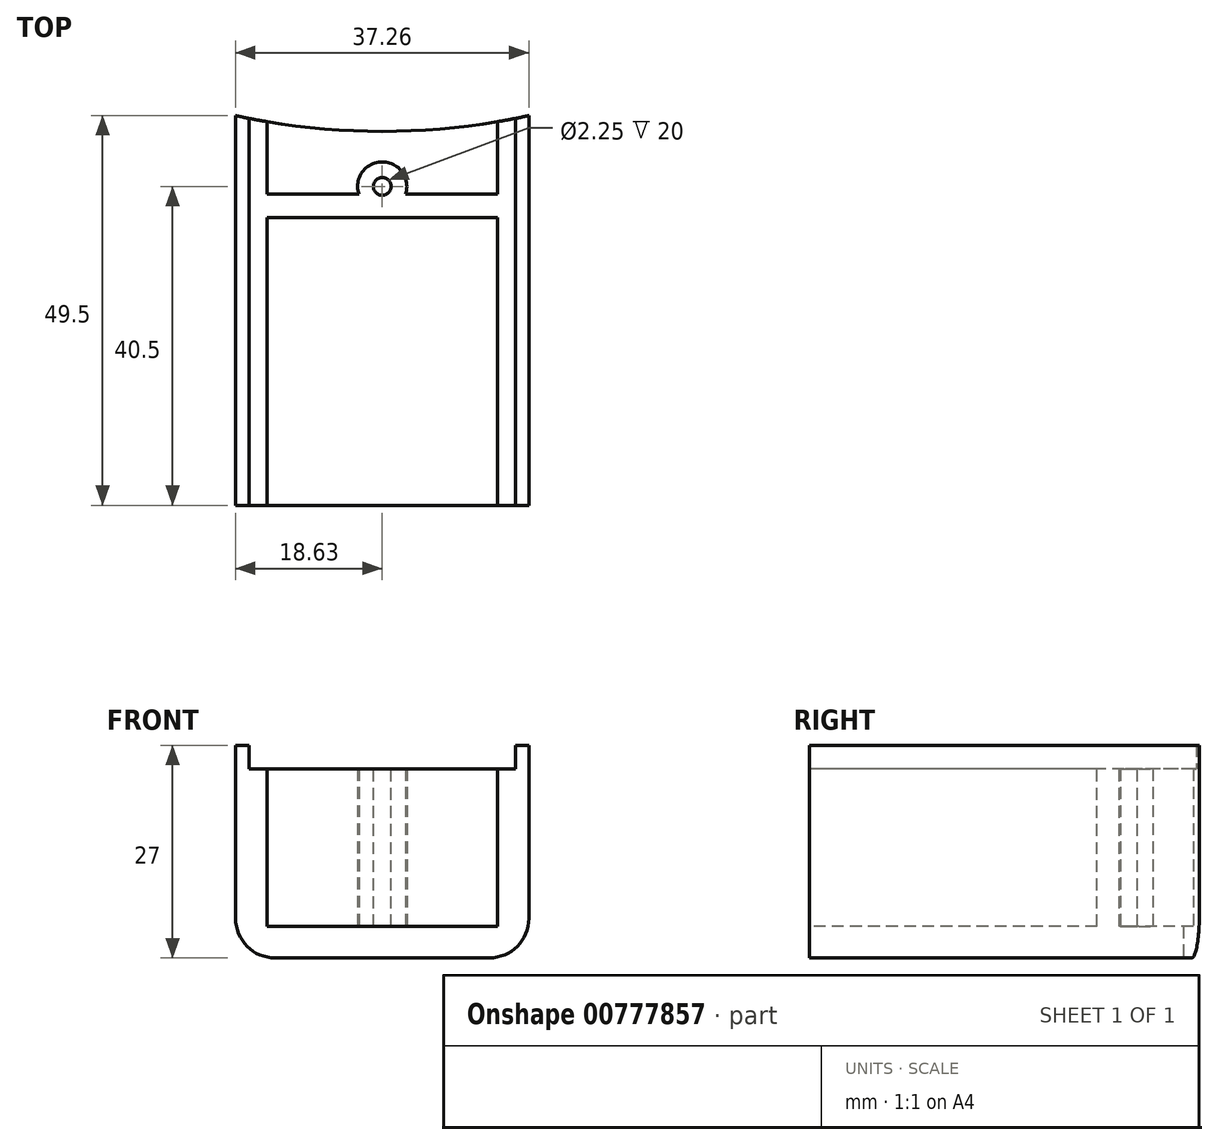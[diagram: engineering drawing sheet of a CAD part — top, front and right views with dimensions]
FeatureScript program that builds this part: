
annotation { "Feature Type Name" : "Feature", "Feature Type Description" : "" }
export const myFeature = defineFeature(function(context is Context, id is Id, definition is map)
    precondition{}
    {
        {
            var Q0;
            Q0=qCreatedBy(makeId("Top.planeOp"),FACE);
            var sketch = newSketch(context, id + "F0", { "sketchPlane" : qUnion([Q0])});
            skLineSegment(sketch, "E0.bottom", {"start": v(18.62, 24.75) * mm, "end": v(-18.63, 24.75) * mm});
            skLineSegment(sketch, "E0.top", {"start": v(18.62, -24.75) * mm, "end": v(-18.63, -24.75) * mm});
            skLineSegment(sketch, "E0.left", {"start": v(18.62, 24.75) * mm, "end": v(18.62, -24.75) * mm});
            skLineSegment(sketch, "E0.right", {"start": v(-18.63, 24.75) * mm, "end": v(-18.63, -24.75) * mm});
            skPoint(sketch, "E0.middle", {"position": v(0, 0) * mm});
            skSolve(sketch);
        }
        {
            var Q0;
            Q0 = qSketchRegion(id + "F0", true);
            extrude(context, id + "F1", {"entities" : qUnion([Q0]), "depth" : 27 * mm, "offsetDistance" : 25 * mm});
        }
        {
            var Q0;
            Q0=makeQuery(id+"F1.opExtrude","SWEPT_FACE",FACE,{"disambiguationData":[OSD([sQuery(id+"F0.wireOp",EDGE,"E0.top")])]});
            var sketch = newSketch(context, id + "F2", { "sketchPlane" : qUnion([Q0])});
            skPoint(sketch, "E1", {"position": v(-14.63, 27) * mm});
            skLineSegment(sketch, "E2.bottom", {"start": v(-14.63, 27) * mm, "end": v(14.62, 27) * mm});
            skLineSegment(sketch, "E2.top", {"start": v(-14.63, 4) * mm, "end": v(14.62, 4) * mm});
            skLineSegment(sketch, "E2.left", {"start": v(-14.63, 27) * mm, "end": v(-14.63, 4) * mm});
            skLineSegment(sketch, "E2.right", {"start": v(14.62, 27) * mm, "end": v(14.62, 4) * mm});
            skSolve(sketch);
        }
        {
            var Q0;
            Q0 = qSketchRegion(id + "F2", true);
            extrude(context, id + "F3", {"entities" : qUnion([Q0]), "operationType" : NewBodyOperationType.REMOVE, "endBound" : BoundingType.THROUGH_ALL, "oppositeDirection" : true, "depth" : 25 * mm, "offsetDistance" : 25 * mm});
        }
        {
            var Q0;
            Q0=makeQuery(id+"F1.opExtrude","SWEPT_FACE",FACE,{"disambiguationData":[OSD([sQuery(id+"F0.wireOp",EDGE,"E0.top")])]});
            var sketch = newSketch(context, id + "F4", { "sketchPlane" : qUnion([Q0])});
            skPoint(sketch, "E3", {"position": v(16.93, 27) * mm});
            skPoint(sketch, "E4", {"position": v(18.62, 27) * mm});
            skPoint(sketch, "E5", {"position": v(-16.93, 27) * mm});
            skPoint(sketch, "E6", {"position": v(-18.63, 27) * mm});
            skLineSegment(sketch, "E7.bottom", {"start": v(-16.93, 27) * mm, "end": v(-14.63, 27) * mm});
            skLineSegment(sketch, "E7.top", {"start": v(-16.93, 24) * mm, "end": v(-14.63, 24) * mm});
            skLineSegment(sketch, "E7.left", {"start": v(-16.93, 27) * mm, "end": v(-16.93, 24) * mm});
            skLineSegment(sketch, "E7.right", {"start": v(-14.63, 27) * mm, "end": v(-14.63, 24) * mm});
            skLineSegment(sketch, "E8.bottom", {"start": v(16.93, 27) * mm, "end": v(14.62, 27) * mm});
            skLineSegment(sketch, "E8.top", {"start": v(16.93, 24) * mm, "end": v(14.62, 24) * mm});
            skLineSegment(sketch, "E8.left", {"start": v(16.93, 27) * mm, "end": v(16.93, 24) * mm});
            skLineSegment(sketch, "E8.right", {"start": v(14.62, 27) * mm, "end": v(14.62, 24) * mm});
            skSolve(sketch);
        }
        {
            var Q0;
            Q0 = qSketchRegion(id + "F4", true);
            extrude(context, id + "F5", {"entities" : qUnion([Q0]), "operationType" : NewBodyOperationType.REMOVE, "endBound" : BoundingType.THROUGH_ALL, "oppositeDirection" : true, "depth" : 25 * mm, "offsetDistance" : 25 * mm});
        }
        {
            var Q0;
            Q0=makeQuery(id+"F1.opExtrude","CAP_EDGE",EDGE,{"disambiguationData":[OSD([sQuery(id+"F0.wireOp",EDGE,"E0.left")])],"isStart":true});
            var Q1;
            Q1=makeQuery(id+"F1.opExtrude","CAP_EDGE",EDGE,{"disambiguationData":[OSD([sQuery(id+"F0.wireOp",EDGE,"E0.right")])],"isStart":true});
            fillet(context, id + "F6", {"entities" : qUnion([Q0, Q1]), "radius" : 5 * mm, "tangentPropagation" : true, "allowEdgeOverflow" : false});
        }
        {
            var Q0;
            Q0=makeQuery(id+"F3.boolean.opBoolean","COPY",FACE,{"derivedFrom":makeQuery(id+"F3.opExtrude","SWEPT_FACE",FACE,{"disambiguationData":[OSD([sQuery(id+"F2.wireOp",EDGE,"E2.top")])]})});
            var sketch = newSketch(context, id + "F7", { "sketchPlane" : qUnion([Q0])});
            skCircle(sketch, "E9", {"center": v(0, 15.75) * mm, "radius": 3.12 * mm});
            skLineSegment(sketch, "E10", {"start": v(0, 15.75) * mm, "end": v(0, 0) * mm, "construction": true});
            skSolve(sketch);
        }
        {
            var Q0;
            Q0=makeQuery(id+"F7.imprint","IMPRINT",FACE,{"disambiguationData":[TD([[makeQuery(id+"F7.imprint","IMPRINT",EDGE,{"derivedFrom":sQuery(id+"F7.wireOp",EDGE,"E9")}),1.0]])]});
            var Q1;
            Q1=makeQuery(id+"F5.boolean.opBoolean","COPY",FACE,{"derivedFrom":makeQuery(id+"F5.opExtrude","SWEPT_FACE",FACE,{"disambiguationData":[OSD([sQuery(id+"F4.wireOp",EDGE,"E8.top")])]})});
            extrude(context, id + "F8", {"entities" : qUnion([Q0]), "operationType" : NewBodyOperationType.ADD, "endBound" : BoundingType.UP_TO_SURFACE, "depth" : 19.7 * mm, "endBoundEntityFace" : qUnion([Q1]), "offsetDistance" : 25 * mm});
        }
        {
            var Q0;
            Q0=makeQuery(id+"F1.opExtrude","CAP_FACE",FACE,{"disambiguationData":[OSD([sQuery(id+"F0.wireOp",EDGE,"E0.bottom"),sQuery(id+"F0.wireOp",EDGE,"E0.top"),sQuery(id+"F0.wireOp",EDGE,"E0.left"),sQuery(id+"F0.wireOp",EDGE,"E0.right")])],"isStart":true});
            var sketch = newSketch(context, id + "F9", { "sketchPlane" : qUnion([Q0])});
            skPoint(sketch, "E11", {"position": v(-18.63, -24.75) * mm});
            skPoint(sketch, "E12", {"position": v(18.62, -24.75) * mm});
            skPoint(sketch, "E13", {"position": v(0, -22.75) * mm});
            skArc(sketch, "E14", {"start": v(18.63, -24.75) * mm, "mid": v(0, -22.75) * mm, "end": v(-18.63, -24.75) * mm});
            skLineSegment(sketch, "E15", {"start": v(-18.63, -24.75) * mm, "end": v(18.63, -24.75) * mm});
            skSolve(sketch);
        }
        {
            var Q0;
            Q0 = qSketchRegion(id + "F9", true);
            extrude(context, id + "F10", {"entities" : qUnion([Q0]), "operationType" : NewBodyOperationType.REMOVE, "endBound" : BoundingType.THROUGH_ALL, "oppositeDirection" : true, "depth" : 25 * mm, "offsetDistance" : 25 * mm});
        }
        {
            var Q0;
            Q0=makeQuery(id+"F3.boolean.opBoolean","COPY",FACE,{"derivedFrom":makeQuery(id+"F3.opExtrude","SWEPT_FACE",FACE,{"disambiguationData":[OSD([sQuery(id+"F2.wireOp",EDGE,"E2.top")])]})});
            var sketch = newSketch(context, id + "F11", { "sketchPlane" : qUnion([Q0])});
            skPoint(sketch, "E16", {"position": v(0, 14.75) * mm});
            skPoint(sketch, "E16.positionSnap0", {"position": v(0, 22.75) * mm});
            skLineSegment(sketch, "E17", {"start": v(0, 14.75) * mm, "end": v(17.76, 14.75) * mm});
            skLineSegment(sketch, "E18", {"start": v(17.76, 14.75) * mm, "end": v(17.76, 11.77) * mm});
            skLineSegment(sketch, "E19", {"start": v(17.76, 11.77) * mm, "end": v(-17.66, 11.77) * mm});
            skLineSegment(sketch, "E20", {"start": v(-17.66, 11.77) * mm, "end": v(-17.66, 14.75) * mm});
            skLineSegment(sketch, "E21", {"start": v(-17.66, 14.75) * mm, "end": v(0, 14.75) * mm});
            skSolve(sketch);
        }
        {
            var Q0;
            Q0 = qSketchRegion(id + "F11", true);
            var Q1;
            {var subQ0=sQuery(id+"F0.wireOp",EDGE,"E0.bottom");var subQ1=sQuery(id+"F0.wireOp",EDGE,"E0.top");var subQ2=sQuery(id+"F0.wireOp",EDGE,"E0.left");Q1=makeQuery(id+"F3.boolean.opBoolean","SPLIT",FACE,{"disambiguationData":[TD([makeQuery(id+"F1.opExtrude","SWEPT_FACE",FACE,{"disambiguationData":[OSD([subQ2])]})])],"derivedFrom":makeQuery(id+"F1.opExtrude","CAP_FACE",FACE,{"disambiguationData":[OSD([subQ0,subQ1,subQ2,sQuery(id+"F0.wireOp",EDGE,"E0.right")])],"isStart":false})});}
            extrude(context, id + "F12", {"entities" : qUnion([Q0]), "operationType" : NewBodyOperationType.ADD, "endBound" : BoundingType.UP_TO_SURFACE, "depth" : 25 * mm, "endBoundEntityFace" : qUnion([Q1]), "offsetDistance" : 25 * mm});
        }
        {
            var Q0;
            Q0=makeQuery(id+"F12.opExtrude","SWEPT_FACE",FACE,{"disambiguationData":[OSD([sQuery(id+"F11.wireOp",EDGE,"E19")])]});
            var sketch = newSketch(context, id + "F13", { "sketchPlane" : qUnion([Q0])});
            skPoint(sketch, "E22", {"position": v(-16.93, 24) * mm});
            skPoint(sketch, "E23", {"position": v(16.93, 27) * mm});
            skLineSegment(sketch, "E24.bottom", {"start": v(-16.93, 24) * mm, "end": v(16.93, 24) * mm});
            skLineSegment(sketch, "E24.top", {"start": v(-16.93, 27) * mm, "end": v(16.93, 27) * mm});
            skLineSegment(sketch, "E24.left", {"start": v(-16.93, 24) * mm, "end": v(-16.93, 27) * mm});
            skLineSegment(sketch, "E24.right", {"start": v(16.93, 24) * mm, "end": v(16.93, 27) * mm});
            skSolve(sketch);
        }
        {
            var Q0;
            Q0 = qSketchRegion(id + "F13", true);
            extrude(context, id + "F14", {"entities" : qUnion([Q0]), "operationType" : NewBodyOperationType.REMOVE, "endBound" : BoundingType.THROUGH_ALL, "oppositeDirection" : true, "depth" : 25 * mm, "offsetDistance" : 25 * mm});
        }
        {
            var Q0;
            {var subQ2=makeQuery(id+"F10.boolean.opBoolean","COPY",FACE,{"derivedFrom":makeQuery(id+"F10.opExtrude","SWEPT_FACE",FACE,{"disambiguationData":[OSD([sQuery(id+"F9.wireOp",EDGE,"E14")])]})});var subQ3=makeQuery(id+"F12.opExtrude","SWEPT_FACE",FACE,{"disambiguationData":[OSD([sQuery(id+"F11.wireOp",EDGE,"E17"),sQuery(id+"F11.wireOp",EDGE,"E21")])]});var subQ4=sQuery(id+"F4.wireOp",EDGE,"E8.top");var subQ5=makeQuery(id+"F5.boolean.opBoolean","COPY",FACE,{"derivedFrom":makeQuery(id+"F5.opExtrude","SWEPT_FACE",FACE,{"disambiguationData":[OSD([subQ4])]})});var subQ6=makeQuery(id+"F1.opExtrude","SWEPT_FACE",FACE,{"disambiguationData":[OSD([sQuery(id+"F0.wireOp",EDGE,"E0.top")])]});var subQ7=makeQuery(id+"F12.opExtrude","SWEPT_FACE",FACE,{"disambiguationData":[OSD([sQuery(id+"F11.wireOp",EDGE,"E19")])]});var subQ10=makeQuery(id+"F5.boolean.opBoolean","COPY",FACE,{"derivedFrom":makeQuery(id+"F5.opExtrude","SWEPT_FACE",FACE,{"disambiguationData":[OSD([sQuery(id+"F4.wireOp",EDGE,"E7.top")])]})});var subQ12=makeQuery(id+"F8.opExtrude","CAP_FACE",FACE,{"disambiguationData":[OSD([subQ4])],"isStart":false});Q0=makeQuery(id+"F14.boolean.opBoolean","MERGE",FACE,{"derivedFrom":[makeQuery(id+"F12.boolean.opBoolean","SPLIT",FACE,{"disambiguationData":[TD([subQ3])],"derivedFrom":subQ12}),makeQuery(id+"F12.boolean.opBoolean","SPLIT",FACE,{"disambiguationData":[TD([subQ7])],"derivedFrom":subQ12}),makeQuery(id+"F12.boolean.opBoolean","SPLIT",FACE,{"disambiguationData":[TD([subQ6])],"derivedFrom":subQ10}),makeQuery(id+"F12.boolean.opBoolean","SPLIT",FACE,{"disambiguationData":[TD([subQ2])],"derivedFrom":subQ10}),makeQuery(id+"F12.boolean.opBoolean","SPLIT",FACE,{"disambiguationData":[TD([subQ6])],"derivedFrom":subQ5}),makeQuery(id+"F12.boolean.opBoolean","SPLIT",FACE,{"disambiguationData":[TD([subQ2])],"derivedFrom":subQ5}),makeQuery(id+"F14.opExtrude","SWEPT_FACE",FACE,{"disambiguationData":[OSD([sQuery(id+"F13.wireOp",EDGE,"E24.bottom")])]})]});}
            var sketch = newSketch(context, id + "F15", { "sketchPlane" : qUnion([Q0])});
            skPoint(sketch, "E25", {"position": v(0, 15.75) * mm});
            skCircle(sketch, "E26", {"center": v(0, 15.75) * mm, "radius": 1.13 * mm});
            skSolve(sketch);
        }
        {
            var Q0;
            Q0 = qSketchRegion(id + "F15", true);
            var Q1;
            Q1=makeQuery(id+"F12.boolean.opBoolean","SPLIT",FACE,{"disambiguationData":[TD([makeQuery(id+"F10.boolean.opBoolean","COPY",FACE,{"derivedFrom":makeQuery(id+"F10.opExtrude","SWEPT_FACE",FACE,{"disambiguationData":[OSD([sQuery(id+"F9.wireOp",EDGE,"E14")])]})})])],"derivedFrom":makeQuery(id+"F3.boolean.opBoolean","COPY",FACE,{"derivedFrom":makeQuery(id+"F3.opExtrude","SWEPT_FACE",FACE,{"disambiguationData":[OSD([sQuery(id+"F2.wireOp",EDGE,"E2.top")])]})})});
            extrude(context, id + "F16", {"entities" : qUnion([Q0]), "operationType" : NewBodyOperationType.REMOVE, "endBound" : BoundingType.UP_TO_SURFACE, "oppositeDirection" : true, "depth" : 25 * mm, "endBoundEntityFace" : qUnion([Q1]), "offsetDistance" : 25 * mm});
        }
    });
